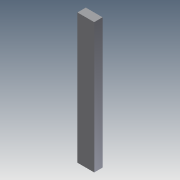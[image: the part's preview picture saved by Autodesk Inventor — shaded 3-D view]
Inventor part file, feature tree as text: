
AUTODESK INVENTOR PART (.ipt)
format: ipt  version: 2011 (Build 150239000, 239)  size: 650,752 bytes
history: native  units: in
note: dims shown in document units (in); Inventor stores cm internally (conversion verified against a paired STEP export)
features: extrude x30, sketch x30
ambient origin geometry x8: Origin, YZ Plane, XZ Plane, XY Plane, X Axis, Y Axis, Z Axis, Center Point
bodies: Solid1 (feature_tree)
feature tree (60):
  extrude  "Extrusion1"  Depth=6.75in
  extrude  "Extrusion2"  Depth=0.5in
  extrude  "Extrusion3"  Depth=0.5in
  extrude  "Extrusion4"  Depth=5.75in
  extrude  "Extrusion5"  Depth=0.5in
  extrude  "Extrusion6"  Depth=1.5in
  extrude  "Extrusion7"  Depth=1.5in
  extrude  "Extrusion8"  Depth=0.156in
  extrude  "Extrusion9"  Depth=0.25in TaperAngle=0.0deg
  extrude  "Extrusion10"  Depth=0.25in TaperAngle=0.0deg
  extrude  "Extrusion11"  Depth=0.25in TaperAngle=0.0deg
  extrude  "Extrusion12"  Depth=0.25in
  extrude  "Extrusion13"  Depth=0.25in
  extrude  "Extrusion14"  Depth=0.25in TaperAngle=0.0deg
  extrude  "Extrusion15"  Depth=3.0in
  extrude  "Extrusion16"  Depth=0.25in TaperAngle=0.0deg
  extrude  "Extrusion17"  Depth=1.0in
  extrude  "Extrusion18"  Depth=0.25in TaperAngle=0.0deg
  extrude  "Extrusion19"  Depth=0.25in TaperAngle=0.0deg
  extrude  "Extrusion20"  Depth=0.25in TaperAngle=0.0deg
  extrude  "Extrusion21"  Depth=1.0in
  extrude  "Extrusion22"  Depth=1.0in
  extrude  "Extrusion23"  Depth=2.0in
  extrude  "Extrusion24"  Depth=0.5in
  extrude  "Extrusion25"  Depth=0.5in
  extrude  "Extrusion26"  Depth=0.5in
  extrude  "Extrusion27"  Depth=0.5in
  extrude  "Extrusion28"  Depth=0.5in
  extrude  "Extrusion29"  Depth=0.5in
  extrude  "Extrusion30"  Depth=0.25in TaperAngle=0.0deg
  sketch  "Sketch1"  dims[d0=5.2in d1=6.75in]
  sketch  "Sketch2"  dims[d2=0.25in d3=0.5in]
  sketch  "Sketch3"  dims[d4=5.7in d5=0.5in]
  sketch  "Sketch4"  dims[d6=0.5in d7=5.75in]
  sketch  "Sketch5"  dims[d8=0.375in d9=0.5in]
  sketch  "Sketch6"  dims[d10=0.25in d11=1.5in]
  sketch  "Sketch7"  dims[d12=0.25in d13=1.5in]
  sketch  "Sketch8"  dims[d14=0.25in d15=0.156in]
  sketch  "Sketch9"  dims[d16=0.156in d17=0.25in d18=0.0in]
  sketch  "Sketch10"  dims[d19=0.125in d20=0.0in d21=0.25in d22=0.0in]
  sketch  "Sketch11"  dims[d23=0.25in d24=0.0in d25=0.25in d26=0.0in]
  sketch  "Sketch12"  dims[d27=0.25in d28=0.25in]
  sketch  "Sketch13"  dims[d29=0.25in d30=0.25in]
  sketch  "Sketch14"  dims[d31=0.25in d32=0.25in d33=0.0in]
  sketch  "Sketch15"  dims[d34=1.5in d35=3.0in]
  sketch  "Sketch16"  dims[d36=1.0in d37=0.25in d38=0.0in]
  sketch  "Sketch17"  dims[d39=6.65in d40=1.0in]
  sketch  "Sketch18"  dims[d41=1.5in d42=0.25in d43=0.0in]
  sketch  "Sketch19"  dims[d44=0.25in d45=0.0in d46=0.25in d47=0.0in]
  sketch  "Sketch20"  dims[d48=1.0in d49=0.25in d50=0.0in]
  sketch  "Sketch21"  dims[d51=0.25in d52=1.0in]
  sketch  "Sketch22"  dims[d53=0.25in d54=1.0in]
  sketch  "Sketch23"  dims[d55=0.25in d56=2.0in]
  sketch  "Sketch24"  dims[d57=1.0in d58=0.5in]
  sketch  "Sketch25"  dims[d59=1.0in d60=0.5in]
  sketch  "Sketch26"  dims[d61=1.0in d62=0.5in]
  sketch  "Sketch27"  dims[d63=1.0in d64=0.5in]
  sketch  "Sketch28"  dims[d65=1.0in d66=0.5in]
  sketch  "Sketch29"  dims[d67=1.0in d68=0.5in]
  sketch  "Sketch30"  dims[d69=1.0in d70=0.25in d71=0.0in d72=0.25in d73=1.0in d74=1.0in d75=0.25in d76=0.0in d77=0.25in d78=0.0in d79=0.25in d80=0.25in d81=0.0in d82=0.75in d83=0.156in d84=0.156in d85=0.25in d86=0.0in d87=0.25in d88=0.0in d89=1.0in d90=1.0in d91=1.0in d92=0.25in d93=0.0in d94=1.0in d95=0.0in d96=1.0in d97=0.0in d98=1.0in d99=0.0in d100=0.5in d101=0.0in d102=0.5in d103=0.0in d104=0.25in d105=0.5in d106=0.0in d107=0.5in d108=0.0in d109=0.25in d110=0.0in d111=0.25in d112=0.0in d113=0.25in d114=0.5in d115=0.0in d116=0.25in d117=0.0in d118=0.5in d119=0.0in]
